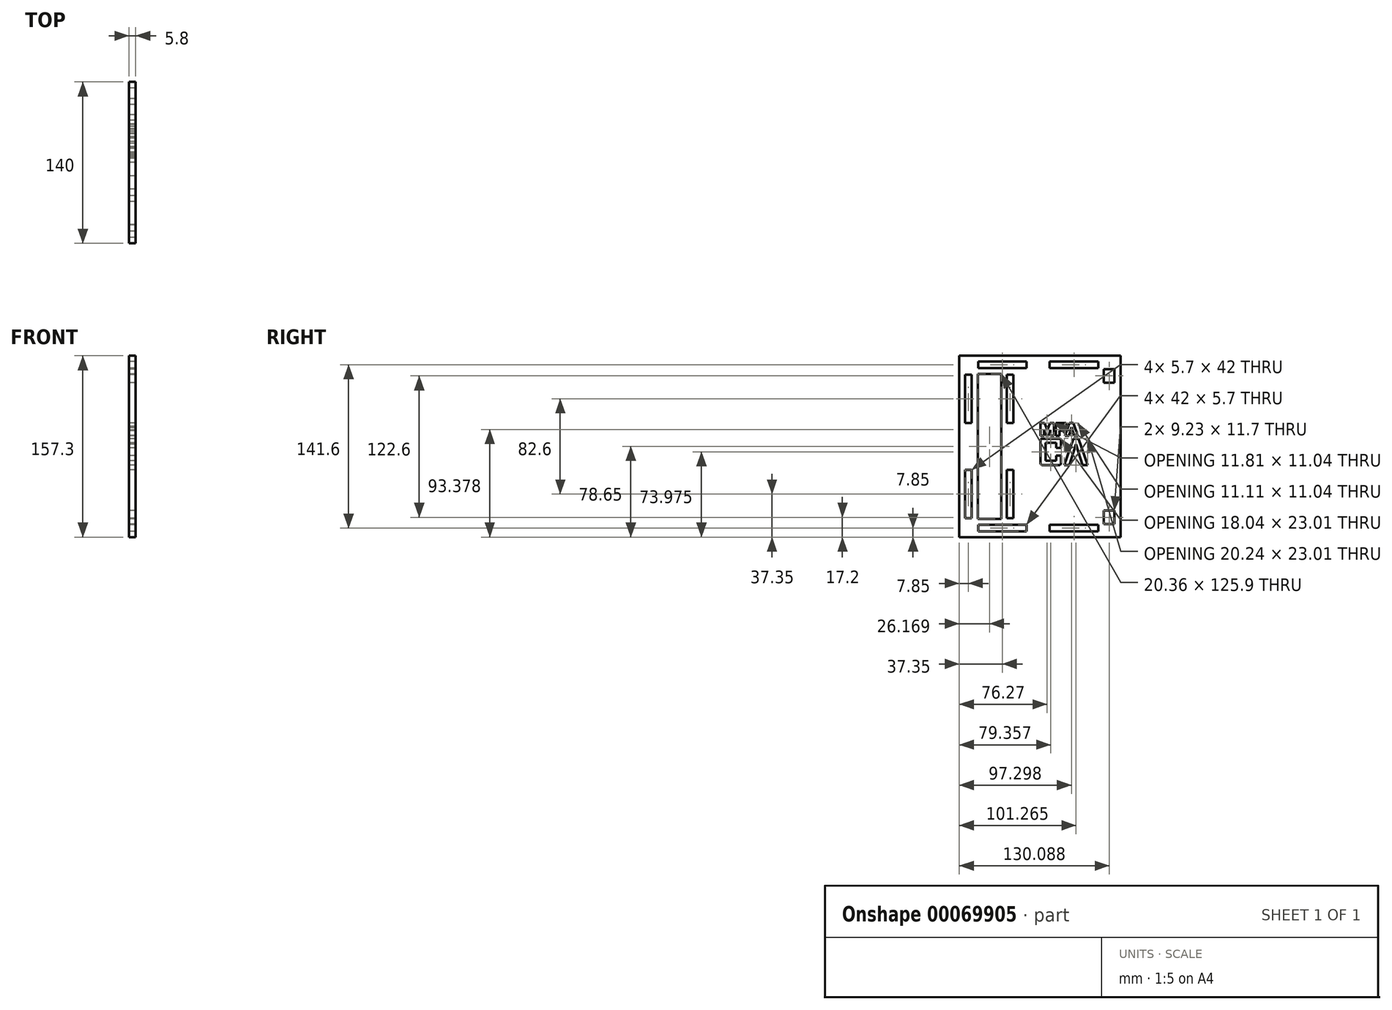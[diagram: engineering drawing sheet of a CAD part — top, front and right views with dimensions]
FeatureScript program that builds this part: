
annotation { "Feature Type Name" : "Feature", "Feature Type Description" : "" }
export const myFeature = defineFeature(function(context is Context, id is Id, definition is map)
    precondition{}
    {
        {
            var Q0;
            Q0=qCreatedBy(makeId("Right.planeOp"),FACE);
            var sketch = newSketch(context, id + "F0", { "sketchPlane" : qUnion([Q0])});
            skLineSegment(sketch, "E0.bottom", {"start": v(70, 78.65) * mm, "end": v(-70, 78.65) * mm});
            skLineSegment(sketch, "E0.top", {"start": v(70, -78.65) * mm, "end": v(-70, -78.65) * mm});
            skLineSegment(sketch, "E0.left", {"start": v(70, 78.65) * mm, "end": v(70, -78.65) * mm});
            skLineSegment(sketch, "E0.right", {"start": v(-70, 78.65) * mm, "end": v(-70, -78.65) * mm});
            skPoint(sketch, "E0.middle", {"position": v(0, 0) * mm});
            skLineSegment(sketch, "E1.bottom", {"start": v(-65, 20.3) * mm, "end": v(-59.3, 20.3) * mm});
            skLineSegment(sketch, "E1.top", {"start": v(-65, 62.3) * mm, "end": v(-59.3, 62.3) * mm});
            skLineSegment(sketch, "E1.left", {"start": v(-65, 20.3) * mm, "end": v(-65, 62.3) * mm});
            skLineSegment(sketch, "E1.right", {"start": v(-59.3, 20.3) * mm, "end": v(-59.3, 62.3) * mm});
            skLineSegment(sketch, "E2.bottom", {"start": v(-65, -62.3) * mm, "end": v(-59.3, -62.3) * mm});
            skLineSegment(sketch, "E2.top", {"start": v(-65, -20.3) * mm, "end": v(-59.3, -20.3) * mm});
            skLineSegment(sketch, "E2.left", {"start": v(-65, -62.3) * mm, "end": v(-65, -20.3) * mm});
            skLineSegment(sketch, "E2.right", {"start": v(-59.3, -62.3) * mm, "end": v(-59.3, -20.3) * mm});
            skLineSegment(sketch, "E3.bottom", {"start": v(-28.65, 62.3) * mm, "end": v(-22.95, 62.3) * mm, "construction": true});
            skLineSegment(sketch, "E3.top", {"start": v(-28.65, 20.3) * mm, "end": v(-22.95, 20.3) * mm, "construction": true});
            skLineSegment(sketch, "E3.left", {"start": v(-28.65, 62.3) * mm, "end": v(-28.65, 20.3) * mm, "construction": true});
            skLineSegment(sketch, "E3.right", {"start": v(-22.95, 62.3) * mm, "end": v(-22.95, 20.3) * mm, "construction": true});
            skLineSegment(sketch, "E4.bottom", {"start": v(-22.95, -62.3) * mm, "end": v(-28.65, -62.3) * mm, "construction": true});
            skLineSegment(sketch, "E4.top", {"start": v(-22.95, -20.3) * mm, "end": v(-28.65, -20.3) * mm, "construction": true});
            skLineSegment(sketch, "E4.left", {"start": v(-22.95, -62.3) * mm, "end": v(-22.95, -20.3) * mm, "construction": true});
            skLineSegment(sketch, "E4.right", {"start": v(-28.65, -62.3) * mm, "end": v(-28.65, -20.3) * mm, "construction": true});
            skLineSegment(sketch, "E5.bottom", {"start": v(-28.65, 62.3) * mm, "end": v(-22.95, 62.3) * mm});
            skLineSegment(sketch, "E5.top", {"start": v(-28.65, 20.3) * mm, "end": v(-22.95, 20.3) * mm});
            skLineSegment(sketch, "E5.left", {"start": v(-28.65, 62.3) * mm, "end": v(-28.65, 20.3) * mm});
            skLineSegment(sketch, "E5.right", {"start": v(-22.95, 62.3) * mm, "end": v(-22.95, 20.3) * mm});
            skLineSegment(sketch, "E6.bottom", {"start": v(-28.65, -20.3) * mm, "end": v(-22.95, -20.3) * mm});
            skLineSegment(sketch, "E6.top", {"start": v(-28.65, -62.3) * mm, "end": v(-22.95, -62.3) * mm});
            skLineSegment(sketch, "E6.left", {"start": v(-28.65, -20.3) * mm, "end": v(-28.65, -62.3) * mm});
            skLineSegment(sketch, "E6.right", {"start": v(-22.95, -20.3) * mm, "end": v(-22.95, -62.3) * mm});
            skLineSegment(sketch, "E7.bottom", {"start": v(-53.65, 73.65) * mm, "end": v(-11.65, 73.65) * mm});
            skLineSegment(sketch, "E7.top", {"start": v(-53.65, 67.95) * mm, "end": v(-11.65, 67.95) * mm});
            skLineSegment(sketch, "E7.left", {"start": v(-53.65, 73.65) * mm, "end": v(-53.65, 67.95) * mm});
            skLineSegment(sketch, "E7.right", {"start": v(-11.65, 73.65) * mm, "end": v(-11.65, 67.95) * mm});
            skLineSegment(sketch, "E8.bottom", {"start": v(-53.65, -67.95) * mm, "end": v(-11.65, -67.95) * mm});
            skLineSegment(sketch, "E8.top", {"start": v(-53.65, -73.65) * mm, "end": v(-11.65, -73.65) * mm});
            skLineSegment(sketch, "E8.left", {"start": v(-53.65, -67.95) * mm, "end": v(-53.65, -73.65) * mm});
            skLineSegment(sketch, "E8.right", {"start": v(-11.65, -67.95) * mm, "end": v(-11.65, -73.65) * mm});
            skLineSegment(sketch, "E9.bottom", {"start": v(64.7, 67) * mm, "end": v(55.47, 67) * mm});
            skLineSegment(sketch, "E9.top", {"start": v(64.7, 55.3) * mm, "end": v(55.47, 55.3) * mm});
            skLineSegment(sketch, "E9.left", {"start": v(64.7, 67) * mm, "end": v(64.7, 55.3) * mm});
            skLineSegment(sketch, "E9.right", {"start": v(55.47, 67) * mm, "end": v(55.47, 55.3) * mm});
            skLineSegment(sketch, "E10.bottom", {"start": v(64.7, -67.3) * mm, "end": v(55.47, -67.3) * mm});
            skLineSegment(sketch, "E10.top", {"start": v(64.7, -55.6) * mm, "end": v(55.48, -55.6) * mm});
            skLineSegment(sketch, "E10.left", {"start": v(64.7, -67.3) * mm, "end": v(64.7, -55.6) * mm});
            skLineSegment(sketch, "E10.right", {"start": v(55.48, -67.3) * mm, "end": v(55.48, -55.6) * mm});
            skLineSegment(sketch, "E11.bottom", {"start": v(8.47, 73.65) * mm, "end": v(50.47, 73.65) * mm});
            skLineSegment(sketch, "E11.top", {"start": v(8.47, 67.95) * mm, "end": v(50.47, 67.95) * mm});
            skLineSegment(sketch, "E11.left", {"start": v(8.47, 73.65) * mm, "end": v(8.47, 67.95) * mm});
            skLineSegment(sketch, "E11.right", {"start": v(50.47, 73.65) * mm, "end": v(50.47, 67.95) * mm});
            skLineSegment(sketch, "E12.bottom", {"start": v(8.48, -67.95) * mm, "end": v(50.48, -67.95) * mm});
            skLineSegment(sketch, "E12.top", {"start": v(8.47, -73.65) * mm, "end": v(50.48, -73.65) * mm});
            skLineSegment(sketch, "E12.left", {"start": v(8.48, -67.95) * mm, "end": v(8.48, -73.65) * mm});
            skLineSegment(sketch, "E12.right", {"start": v(50.48, -67.95) * mm, "end": v(50.48, -73.65) * mm});
            skLineSegment(sketch, "E13.bottom", {"start": v(-33.65, 62.95) * mm, "end": v(-54.01, 62.95) * mm});
            skLineSegment(sketch, "E13.top", {"start": v(-33.65, -62.95) * mm, "end": v(-54.01, -62.95) * mm});
            skLineSegment(sketch, "E13.left", {"start": v(-33.65, 62.95) * mm, "end": v(-33.65, -62.95) * mm});
            skLineSegment(sketch, "E13.right", {"start": v(-54.01, 62.95) * mm, "end": v(-54.01, -62.95) * mm});
            skPoint(sketch, "E13.middle", {"position": v(-43.83, 0) * mm});
            skLineSegment(sketch, "E14", {"start": v(16.58, -16.18) * mm, "end": v(2.14, -16.18) * mm});
            skLineSegment(sketch, "E15", {"start": v(0.34, -14.38) * mm, "end": v(0.34, 5.03) * mm});
            skLineSegment(sketch, "E16", {"start": v(2.14, 6.83) * mm, "end": v(16.58, 6.83) * mm});
            skLineSegment(sketch, "E17", {"start": v(18.38, 5.03) * mm, "end": v(18.38, -1.15) * mm});
            skLineSegment(sketch, "E18", {"start": v(18.38, -1.15) * mm, "end": v(13.95, -1.15) * mm});
            skLineSegment(sketch, "E19", {"start": v(13.95, -1.15) * mm, "end": v(13.95, 3.18) * mm});
            skLineSegment(sketch, "E20", {"start": v(13.95, 3.18) * mm, "end": v(4.76, 3.18) * mm});
            skLineSegment(sketch, "E21", {"start": v(4.76, 3.18) * mm, "end": v(4.76, -12.54) * mm});
            skLineSegment(sketch, "E22", {"start": v(4.76, -12.54) * mm, "end": v(13.95, -12.54) * mm});
            skLineSegment(sketch, "E23", {"start": v(13.95, -12.54) * mm, "end": v(13.95, -7.93) * mm});
            skLineSegment(sketch, "E24", {"start": v(13.95, -7.93) * mm, "end": v(18.38, -7.93) * mm});
            skLineSegment(sketch, "E25", {"start": v(18.38, -7.93) * mm, "end": v(18.38, -14.38) * mm});
            skLineSegment(sketch, "E26", {"start": v(21.15, -16.12) * mm, "end": v(28.92, 6.83) * mm});
            skLineSegment(sketch, "E27", {"start": v(28.92, 6.83) * mm, "end": v(33.61, 6.83) * mm});
            skLineSegment(sketch, "E28", {"start": v(33.61, 6.83) * mm, "end": v(41.38, -16.12) * mm});
            skLineSegment(sketch, "E29", {"start": v(41.38, -16.12) * mm, "end": v(36.84, -16.18) * mm});
            skLineSegment(sketch, "E30", {"start": v(36.84, -16.18) * mm, "end": v(31.23, 1.8) * mm});
            skLineSegment(sketch, "E31", {"start": v(31.23, 1.8) * mm, "end": v(25.66, -16.18) * mm});
            skLineSegment(sketch, "E32", {"start": v(25.66, -16.18) * mm, "end": v(21.15, -16.12) * mm});
            skLineSegment(sketch, "E33", {"start": v(0.37, 9.2) * mm, "end": v(3.57, 9.2) * mm});
            skLineSegment(sketch, "E34", {"start": v(3.57, 9.2) * mm, "end": v(3.57, 14.14) * mm});
            skLineSegment(sketch, "E35", {"start": v(3.57, 14.14) * mm, "end": v(4.98, 9.68) * mm});
            skLineSegment(sketch, "E36", {"start": v(4.98, 9.68) * mm, "end": v(7.6, 9.68) * mm});
            skLineSegment(sketch, "E37", {"start": v(7.6, 9.68) * mm, "end": v(9, 14.14) * mm});
            skLineSegment(sketch, "E38", {"start": v(9, 14.14) * mm, "end": v(9, 9.2) * mm});
            skLineSegment(sketch, "E39", {"start": v(9, 9.2) * mm, "end": v(12.17, 9.2) * mm});
            skLineSegment(sketch, "E40", {"start": v(12.17, 9.2) * mm, "end": v(12.17, 20.25) * mm});
            skLineSegment(sketch, "E41", {"start": v(12.17, 20.25) * mm, "end": v(8.73, 20.25) * mm});
            skLineSegment(sketch, "E42", {"start": v(8.73, 20.25) * mm, "end": v(6.32, 14.32) * mm});
            skLineSegment(sketch, "E43", {"start": v(6.32, 14.32) * mm, "end": v(3.83, 20.25) * mm});
            skLineSegment(sketch, "E44", {"start": v(3.83, 20.25) * mm, "end": v(0.37, 20.25) * mm});
            skLineSegment(sketch, "E45", {"start": v(0.37, 20.25) * mm, "end": v(0.37, 9.2) * mm});
            skLineSegment(sketch, "E46", {"start": v(16.9, 9.2) * mm, "end": v(13.63, 9.2) * mm});
            skLineSegment(sketch, "E47", {"start": v(13.63, 9.2) * mm, "end": v(13.63, 20.25) * mm});
            skLineSegment(sketch, "E48", {"start": v(13.63, 20.25) * mm, "end": v(22.54, 20.25) * mm});
            skLineSegment(sketch, "E49", {"start": v(22.54, 20.25) * mm, "end": v(22.54, 17.59) * mm});
            skLineSegment(sketch, "E50", {"start": v(22.54, 17.59) * mm, "end": v(16.9, 17.59) * mm});
            skLineSegment(sketch, "E51", {"start": v(16.9, 17.59) * mm, "end": v(16.9, 16.09) * mm});
            skLineSegment(sketch, "E52", {"start": v(16.9, 16.09) * mm, "end": v(21.26, 16.09) * mm});
            skLineSegment(sketch, "E53", {"start": v(21.26, 16.09) * mm, "end": v(21.26, 13.57) * mm});
            skLineSegment(sketch, "E54", {"start": v(21.26, 13.57) * mm, "end": v(16.9, 13.57) * mm});
            skLineSegment(sketch, "E55", {"start": v(16.9, 13.57) * mm, "end": v(16.9, 9.2) * mm});
            skLineSegment(sketch, "E56", {"start": v(21.74, 9.24) * mm, "end": v(25.07, 9.2) * mm});
            skLineSegment(sketch, "E57", {"start": v(25.07, 9.2) * mm, "end": v(27.3, 16.72) * mm});
            skLineSegment(sketch, "E58", {"start": v(27.3, 16.72) * mm, "end": v(29.5, 9.2) * mm});
            skLineSegment(sketch, "E59", {"start": v(29.5, 9.2) * mm, "end": v(32.86, 9.24) * mm});
            skLineSegment(sketch, "E60", {"start": v(32.86, 9.24) * mm, "end": v(29.04, 20.25) * mm});
            skLineSegment(sketch, "E61", {"start": v(29.04, 20.25) * mm, "end": v(25.56, 20.25) * mm});
            skLineSegment(sketch, "E62", {"start": v(25.56, 20.25) * mm, "end": v(21.74, 9.24) * mm});
            skPoint(sketch, "E63.visualSharp", {"position": v(0.34, 6.83) * mm});
            skArc(sketch, "E63.filletArc", {"start": v(2.14, 6.83) * mm, "mid": v(0.86, 6.3) * mm, "end": v(0.34, 5.03) * mm});
            skPoint(sketch, "E64.visualSharp", {"position": v(18.38, 6.83) * mm});
            skArc(sketch, "E64.filletArc", {"start": v(18.38, 5.03) * mm, "mid": v(17.85, 6.3) * mm, "end": v(16.58, 6.83) * mm});
            skPoint(sketch, "E65.visualSharp", {"position": v(18.38, -16.18) * mm});
            skArc(sketch, "E65.filletArc", {"start": v(16.58, -16.18) * mm, "mid": v(17.85, -15.65) * mm, "end": v(18.38, -14.38) * mm});
            skPoint(sketch, "E66.visualSharp", {"position": v(0.34, -16.18) * mm});
            skArc(sketch, "E66.filletArc", {"start": v(0.34, -14.38) * mm, "mid": v(0.86, -15.65) * mm, "end": v(2.14, -16.18) * mm});
            skSolve(sketch);
        }
        {
            var Q0;
            Q0=makeQuery(id+"F0.imprint","IMPRINT",FACE,{"disambiguationData":[TD([[makeQuery(id+"F0.imprint","IMPRINT",EDGE,{"derivedFrom":sQuery(id+"F0.wireOp",EDGE,"E0.bottom")}),1.0]])]});
            extrude(context, id + "F1", {"entities" : qUnion([Q0]), "depth" : 5.8 * mm});
        }
    });
